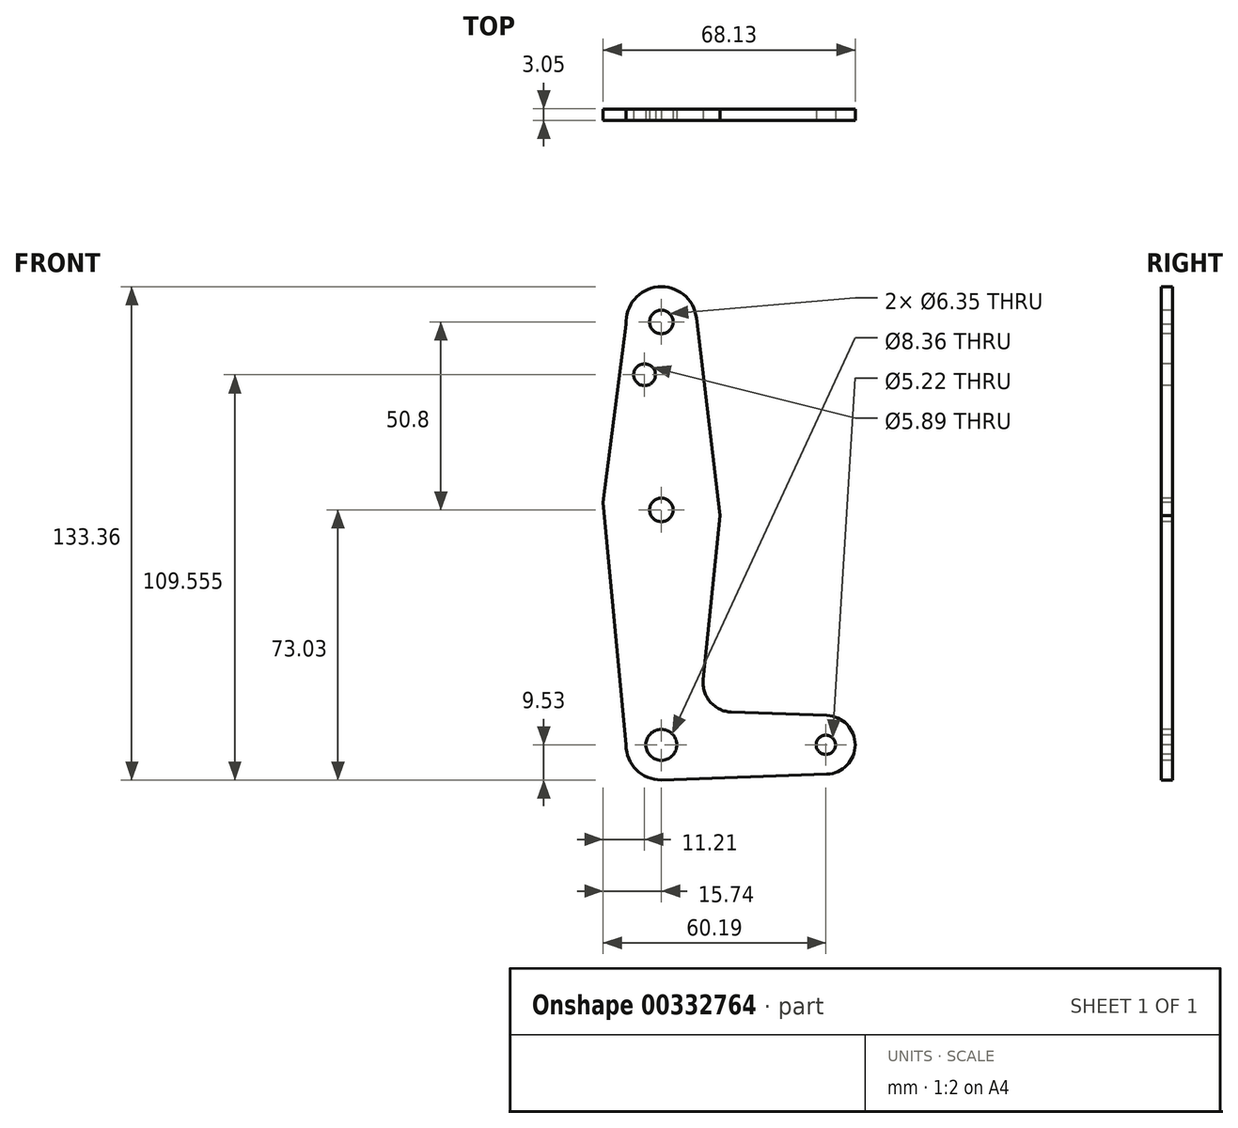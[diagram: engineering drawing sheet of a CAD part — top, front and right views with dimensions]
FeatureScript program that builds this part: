
annotation { "Feature Type Name" : "Feature", "Feature Type Description" : "" }
export const myFeature = defineFeature(function(context is Context, id is Id, definition is map)
    precondition{}
    {
        {
            var Q0;
            Q0=qCreatedBy(makeId("Front.planeOp"),FACE);
            var sketch = newSketch(context, id + "F0", { "sketchPlane" : qUnion([Q0])});
            skLineSegment(sketch, "E0", {"start": v(0, 114.3) * mm, "end": v(0, 0) * mm, "construction": true});
            skCircle(sketch, "E1", {"center": v(0, 114.3) * mm, "radius": 9.53 * mm});
            skCircle(sketch, "E2", {"center": v(0, 63.5) * mm, "radius": 15.88 * mm});
            skCircle(sketch, "E3", {"center": v(0, 0) * mm, "radius": 9.53 * mm});
            skLineSegment(sketch, "E4", {"start": v(0, 0) * mm, "end": v(44.45, 0) * mm, "construction": true});
            skCircle(sketch, "E5", {"center": v(44.45, 0) * mm, "radius": 7.94 * mm});
            skLineSegment(sketch, "E6", {"start": v(-9.5, 113.6) * mm, "end": v(-15.74, 65.55) * mm});
            skLineSegment(sketch, "E7", {"start": v(-9.53, 0) * mm, "end": v(-15.74, 65.55) * mm});
            skLineSegment(sketch, "E8", {"start": v(11.3, 17.6) * mm, "end": v(15.8, 61.9) * mm});
            skLineSegment(sketch, "E9", {"start": v(15.8, 61.9) * mm, "end": v(9.46, 115.42) * mm});
            skLineSegment(sketch, "E10", {"start": v(18.93, 8.85) * mm, "end": v(44.73, 7.93) * mm});
            skLineSegment(sketch, "E11", {"start": v(0, -9.53) * mm, "end": v(44.73, -7.93) * mm});
            skLineSegment(sketch, "E12", {"start": v(-15.74, 65.55) * mm, "end": v(-15.74, 65.55) * mm});
            skCircle(sketch, "E13", {"center": v(0, 114.3) * mm, "radius": 3.18 * mm});
            skCircle(sketch, "E14", {"center": v(0, 63.5) * mm, "radius": 3.17 * mm});
            skCircle(sketch, "E15", {"center": v(0, 0) * mm, "radius": 4.18 * mm});
            skCircle(sketch, "E16", {"center": v(44.45, 0) * mm, "radius": 2.61 * mm});
            skArc(sketch, "E17.filletArc", {"start": v(11.3, 17.6) * mm, "mid": v(13.22, 11.57) * mm, "end": v(18.93, 8.85) * mm});
            skCircle(sketch, "E18", {"center": v(-4.53, 100.03) * mm, "radius": 2.94 * mm});
            skSolve(sketch);
        }
        {
            var Q0;
            {var subQ0=sQuery(id+"F0.wireOp",EDGE,"E6");Q0=makeQuery(id+"F0.imprint","IMPRINT",FACE,{"disambiguationData":[TD([[makeQuery(id+"F0.imprint","IMPRINT",EDGE,{"derivedFrom":subQ0}),1.0]])]});}
            var Q1;
            Q1=makeQuery(id+"F0.imprint","IMPRINT",FACE,{"disambiguationData":[TD([[makeQuery(id+"F0.imprint","IMPRINT",EDGE,{"derivedFrom":sQuery(id+"F0.wireOp",EDGE,"E14")}),-1.0]])]});
            var Q2;
            {var subQ10=sQuery(id+"F0.wireOp",EDGE,"E8");Q2=makeQuery(id+"F0.imprint","IMPRINT",FACE,{"disambiguationData":[TD([[makeQuery(id+"F0.imprint","IMPRINT",EDGE,{"derivedFrom":subQ10}),1.0]])]});}
            var Q3;
            Q3=makeQuery(id+"F0.imprint","IMPRINT",FACE,{"disambiguationData":[TD([[makeQuery(id+"F0.imprint","IMPRINT",EDGE,{"derivedFrom":sQuery(id+"F0.wireOp",EDGE,"E16")}),-1.0]])]});
            var Q4;
            Q4=makeQuery(id+"F0.imprint","IMPRINT",FACE,{"disambiguationData":[TD([[makeQuery(id+"F0.imprint","IMPRINT",EDGE,{"derivedFrom":sQuery(id+"F0.wireOp",EDGE,"E15")}),-1.0]])]});
            var Q5;
            Q5=makeQuery(id+"F0.imprint","IMPRINT",FACE,{"disambiguationData":[TD([[makeQuery(id+"F0.imprint","IMPRINT",EDGE,{"derivedFrom":sQuery(id+"F0.wireOp",EDGE,"E13")}),-1.0]])]});
            extrude(context, id + "F1", {"entities" : qUnion([Q0, Q1, Q2, Q3, Q4, Q5]), "oppositeDirection" : true, "depth" : 3.05 * mm});
        }
    });
